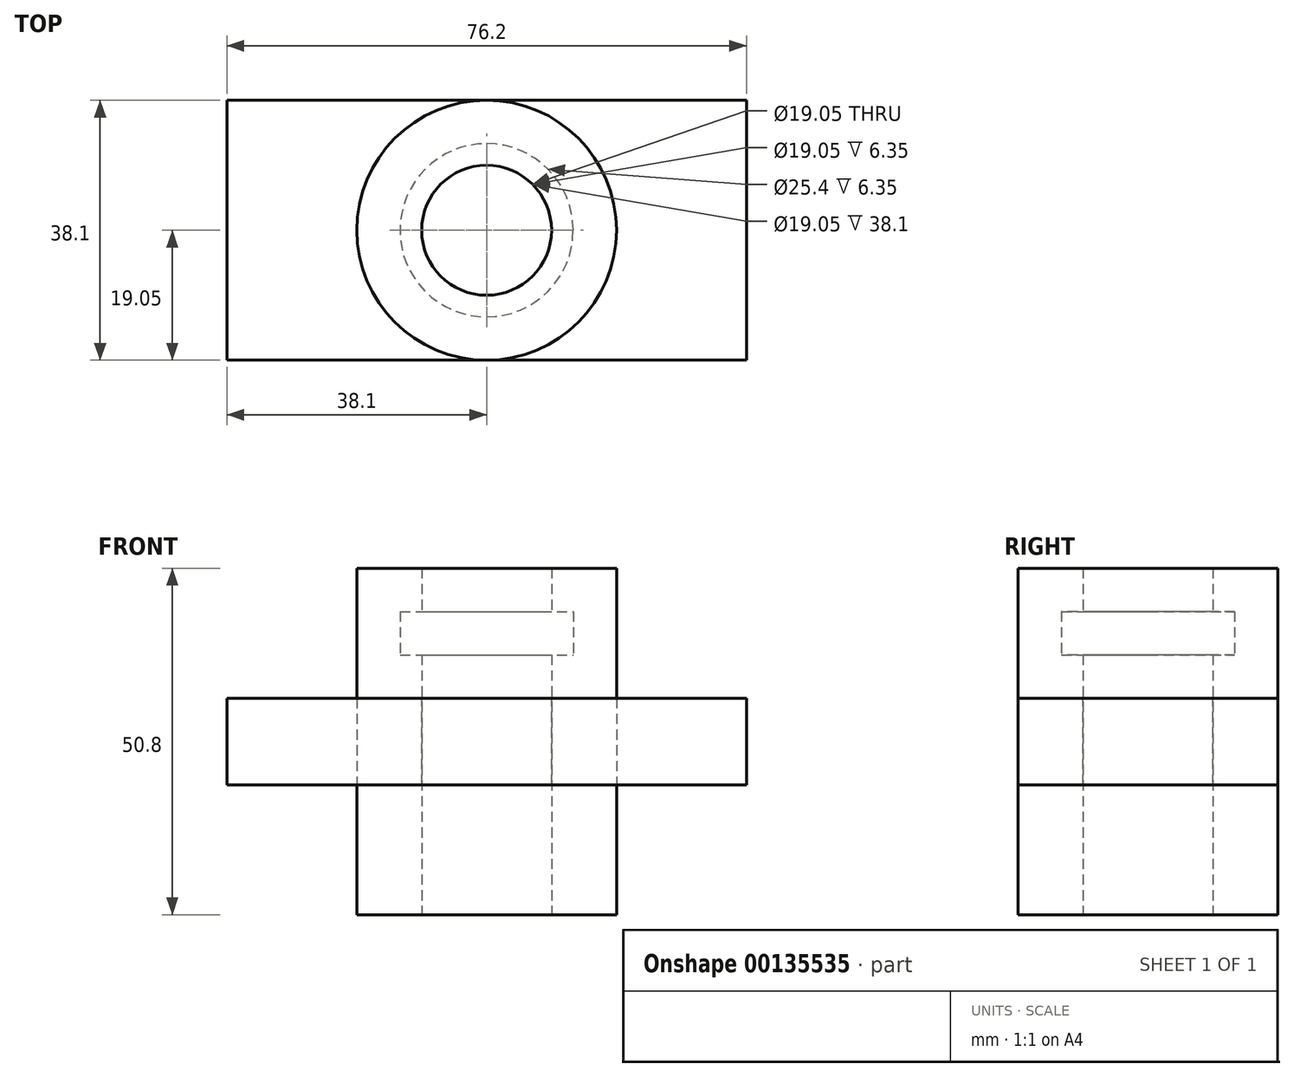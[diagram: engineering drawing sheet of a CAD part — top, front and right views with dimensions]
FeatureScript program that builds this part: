
annotation { "Feature Type Name" : "Feature", "Feature Type Description" : "" }
export const myFeature = defineFeature(function(context is Context, id is Id, definition is map)
    precondition{}
    {
        {
            var Q0;
            Q0=qCreatedBy(makeId("Front.planeOp"),FACE);
            var sketch = newSketch(context, id + "F0", { "sketchPlane" : qUnion([Q0])});
            skLineSegment(sketch, "E0", {"start": v(0, 0) * mm, "end": v(0, 50.8) * mm});
            skLineSegment(sketch, "E1", {"start": v(0, 50.8) * mm, "end": v(19.05, 50.8) * mm});
            skLineSegment(sketch, "E2", {"start": v(19.05, 50.8) * mm, "end": v(19.05, 0) * mm});
            skLineSegment(sketch, "E3", {"start": v(19.05, 0) * mm, "end": v(0, 0) * mm});
            skLineSegment(sketch, "E4", {"start": v(0, 0) * mm, "end": v(0, 0) * mm});
            skLineSegment(sketch, "E5", {"start": v(9.53, 50.8) * mm, "end": v(9.53, 44.45) * mm});
            skLineSegment(sketch, "E6", {"start": v(0, 44.45) * mm, "end": v(12.7, 44.45) * mm});
            skLineSegment(sketch, "E7", {"start": v(12.7, 44.45) * mm, "end": v(12.7, 38.1) * mm});
            skLineSegment(sketch, "E8", {"start": v(12.7, 38.1) * mm, "end": v(0, 38.1) * mm});
            skLineSegment(sketch, "E9", {"start": v(0, 44.45) * mm, "end": v(0, 38.1) * mm});
            skLineSegment(sketch, "E10.trimOffspring", {"start": v(9.53, 38.1) * mm, "end": v(9.53, 0) * mm});
            skLineSegment(sketch, "E11.MirrorCS", {"start": v(38.1, 31.75) * mm, "end": v(-38.1, 31.75) * mm});
            skLineSegment(sketch, "E12.MirrorCS", {"start": v(-38.1, 19.05) * mm, "end": v(38.1, 19.05) * mm});
            skLineSegment(sketch, "E13.MirrorCS", {"start": v(-38.1, 31.75) * mm, "end": v(-38.1, 19.05) * mm});
            skLineSegment(sketch, "E14", {"start": v(38.1, 31.75) * mm, "end": v(38.1, 19.05) * mm});
            skSolve(sketch);
        }
        {
            var Q0;
            {var subQ1=sQuery(id+"F0.wireOp",EDGE,"E5");Q0=makeQuery(id+"F0.imprint","IMPRINT",FACE,{"disambiguationData":[TD([[makeQuery(id+"F0.imprint","IMPRINT",EDGE,{"derivedFrom":subQ1}),1.0]])]});}
            var Q1;
            {var subQ0=sQuery(id+"F0.wireOp",EDGE,"E3");var subQ1=sQuery(id+"F0.wireOp",EDGE,"E2");var subQ2=makeQuery(id+"F0.imprint","INTERSECT",VERTEX,{"derivedFrom":[subQ1,subQ0]});Q1=makeQuery(id+"F0.imprint","IMPRINT",FACE,{"disambiguationData":[TD([[makeQuery(id+"F0.imprint","IMPRINT",EDGE,{"disambiguationData":[TD([[subQ2,1.0]])],"derivedFrom":subQ1}),-1.0]])]});}
            var Q2;
            {var subQ0=sQuery(id+"F0.wireOp",EDGE,"E11.MirrorCS");var subQ1=sQuery(id+"F0.wireOp",EDGE,"E2");var subQ2=makeQuery(id+"F0.imprint","INTERSECT",VERTEX,{"derivedFrom":[subQ1,subQ0]});Q2=makeQuery(id+"F0.imprint","IMPRINT",FACE,{"disambiguationData":[TD([[makeQuery(id+"F0.imprint","IMPRINT",EDGE,{"disambiguationData":[TD([[subQ2,-1.0]])],"derivedFrom":subQ1}),-1.0]])]});}
            var Q3;
            Q3=sQuery(id+"F0.wireOp",EDGE,"E0");
            revolve(context, id + "F1", {"entities" : qUnion([Q0, Q1, Q2]), "axis" : qUnion([Q3]), "revolveType" : RevolveType.FULL});
        }
        {
            var Q0;
            {var subQ5=sQuery(id+"F0.wireOp",EDGE,"E13.MirrorCS");Q0=makeQuery(id+"F0.imprint","IMPRINT",FACE,{"disambiguationData":[TD([[makeQuery(id+"F0.imprint","IMPRINT",EDGE,{"derivedFrom":subQ5}),1.0]])]});}
            var Q1;
            {var subQ5=sQuery(id+"F0.wireOp",EDGE,"E14");Q1=makeQuery(id+"F0.imprint","IMPRINT",FACE,{"disambiguationData":[TD([[makeQuery(id+"F0.imprint","IMPRINT",EDGE,{"derivedFrom":subQ5}),-1.0]])]});}
            var Q2;
            {var subQ0=sQuery(id+"F0.wireOp",EDGE,"E12.MirrorCS");var subQ1=sQuery(id+"F0.wireOp",EDGE,"E0");var subQ2=makeQuery(id+"F0.imprint","INTERSECT",VERTEX,{"derivedFrom":[subQ1,subQ0]});Q2=makeQuery(id+"F0.imprint","IMPRINT",FACE,{"disambiguationData":[TD([[makeQuery(id+"F0.imprint","IMPRINT",EDGE,{"disambiguationData":[TD([[subQ2,-1.0]])],"derivedFrom":subQ1}),-1.0]])]});}
            var Q3;
            {var subQ0=sQuery(id+"F0.wireOp",EDGE,"E11.MirrorCS");var subQ1=sQuery(id+"F0.wireOp",EDGE,"E2");var subQ2=makeQuery(id+"F0.imprint","INTERSECT",VERTEX,{"derivedFrom":[subQ1,subQ0]});Q3=makeQuery(id+"F0.imprint","IMPRINT",FACE,{"disambiguationData":[TD([[makeQuery(id+"F0.imprint","IMPRINT",EDGE,{"disambiguationData":[TD([[subQ2,-1.0]])],"derivedFrom":subQ1}),-1.0]])]});}
            extrude(context, id + "F2", {"entities" : qUnion([Q0, Q1, Q2, Q3]), "endBound" : BoundingType.SYMMETRIC, "depth" : 38.1 * mm});
        }
        {
            var Q0;
            Q0=makeQuery(id+"F2.opExtrude","SWEPT_FACE",FACE,{"disambiguationData":[OSD([sQuery(id+"F0.wireOp",EDGE,"E11.MirrorCS")])]});
            var sketch = newSketch(context, id + "F3", { "sketchPlane" : qUnion([Q0])});
            skCircle(sketch, "E15", {"center": v(0, 0) * mm, "radius": 9.53 * mm});
            skSolve(sketch);
        }
        {
            var Q0;
            Q0 = qSketchRegion(id + "F3", true);
            extrude(context, id + "F4", {"entities" : qUnion([Q0]), "operationType" : NewBodyOperationType.REMOVE, "endBound" : BoundingType.THROUGH_ALL, "oppositeDirection" : true, "depth" : 25.4 * mm});
        }
    });
